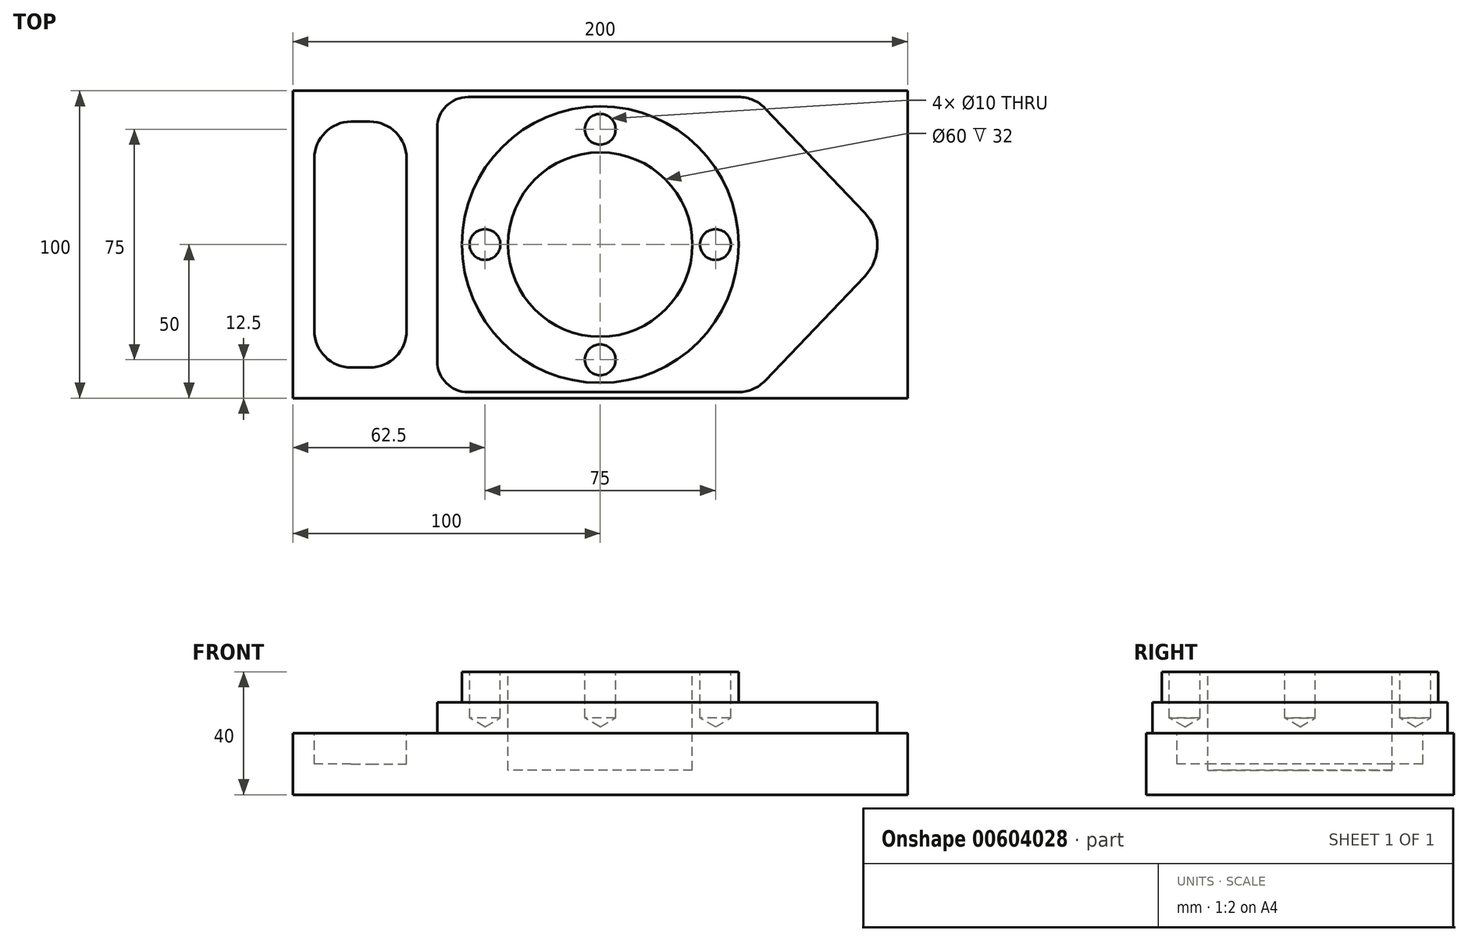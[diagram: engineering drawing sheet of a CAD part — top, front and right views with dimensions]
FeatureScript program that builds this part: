
annotation { "Feature Type Name" : "Feature", "Feature Type Description" : "" }
export const myFeature = defineFeature(function(context is Context, id is Id, definition is map)
    precondition{}
    {
        {
            var Q0;
            Q0=qCreatedBy(makeId("Top.planeOp"),FACE);
            var sketch = newSketch(context, id + "F0", { "sketchPlane" : qUnion([Q0])});
            skLineSegment(sketch, "E0.bottom", {"start": v(-100, 50) * mm, "end": v(100, 50) * mm});
            skLineSegment(sketch, "E0.top", {"start": v(-100, -50) * mm, "end": v(100, -50) * mm});
            skLineSegment(sketch, "E0.left", {"start": v(-100, 50) * mm, "end": v(-100, -50) * mm});
            skLineSegment(sketch, "E0.right", {"start": v(100, 50) * mm, "end": v(100, -50) * mm});
            skPoint(sketch, "E0.middle", {"position": v(0, 0) * mm});
            skSolve(sketch);
        }
        {
            var Q0;
            Q0=makeQuery(id+"F0.imprint","IMPRINT",FACE,{"disambiguationData":[TD([[makeQuery(id+"F0.imprint","IMPRINT",EDGE,{"derivedFrom":sQuery(id+"F0.wireOp",EDGE,"E0.bottom")}),-1.0]])]});
            extrude(context, id + "F1", {"entities" : qUnion([Q0]), "depth" : 20 * mm, "offsetDistance" : 25 * mm});
        }
        {
            var Q0;
            Q0=makeQuery(id+"F1.opExtrude","CAP_FACE",FACE,{"disambiguationData":[OSD([sQuery(id+"F0.wireOp",EDGE,"E0.bottom"),sQuery(id+"F0.wireOp",EDGE,"E0.top"),sQuery(id+"F0.wireOp",EDGE,"E0.left"),sQuery(id+"F0.wireOp",EDGE,"E0.right")])],"isStart":false});
            var sketch = newSketch(context, id + "F2", { "sketchPlane" : qUnion([Q0])});
            skLineSegment(sketch, "E1.bottom", {"start": v(-81, 40) * mm, "end": v(-75, 40) * mm});
            skLineSegment(sketch, "E1.top", {"start": v(-81, -40) * mm, "end": v(-75, -40) * mm});
            skLineSegment(sketch, "E1.left", {"start": v(-93, 28) * mm, "end": v(-93, -28) * mm});
            skLineSegment(sketch, "E1.right", {"start": v(-63, 28) * mm, "end": v(-63, -28) * mm});
            skPoint(sketch, "E2.visualSharp", {"position": v(-93, 40) * mm});
            skArc(sketch, "E2.filletArc", {"start": v(-81, 40) * mm, "mid": v(-89.49, 36.49) * mm, "end": v(-93, 28) * mm});
            skPoint(sketch, "E3.visualSharp", {"position": v(-63, 40) * mm});
            skArc(sketch, "E3.filletArc", {"start": v(-63, 28) * mm, "mid": v(-66.51, 36.49) * mm, "end": v(-75, 40) * mm});
            skPoint(sketch, "E4.visualSharp", {"position": v(-93, -40) * mm});
            skArc(sketch, "E4.filletArc", {"start": v(-93, -28) * mm, "mid": v(-89.49, -36.49) * mm, "end": v(-81, -40) * mm});
            skPoint(sketch, "E5.visualSharp", {"position": v(-63, -40) * mm});
            skArc(sketch, "E5.filletArc", {"start": v(-75, -40) * mm, "mid": v(-66.51, -36.49) * mm, "end": v(-63, -28) * mm});
            skSolve(sketch);
        }
        {
            var Q0;
            Q0=makeQuery(id+"F2.imprint","IMPRINT",FACE,{"disambiguationData":[TD([[makeQuery(id+"F2.imprint","IMPRINT",EDGE,{"derivedFrom":sQuery(id+"F2.wireOp",EDGE,"E1.bottom")}),-1.0]])]});
            extrude(context, id + "F3", {"entities" : qUnion([Q0]), "operationType" : NewBodyOperationType.REMOVE, "oppositeDirection" : true, "depth" : 10 * mm, "offsetDistance" : 25 * mm});
        }
        {
            var Q0;
            Q0=makeQuery(id+"F1.opExtrude","CAP_FACE",FACE,{"disambiguationData":[OSD([sQuery(id+"F0.wireOp",EDGE,"E0.bottom"),sQuery(id+"F0.wireOp",EDGE,"E0.top"),sQuery(id+"F0.wireOp",EDGE,"E0.left"),sQuery(id+"F0.wireOp",EDGE,"E0.right")])],"isStart":false});
            var sketch = newSketch(context, id + "F4", { "sketchPlane" : qUnion([Q0])});
            skLineSegment(sketch, "E6.bottom", {"start": v(-43, 48) * mm, "end": v(45.03, 48) * mm});
            skLineSegment(sketch, "E6.top", {"start": v(-43, -48) * mm, "end": v(45.03, -48) * mm});
            skLineSegment(sketch, "E6.left", {"start": v(-53, 38) * mm, "end": v(-53, -38) * mm});
            skPoint(sketch, "E7.visualSharp", {"position": v(-53, 48) * mm});
            skArc(sketch, "E7.filletArc", {"start": v(-43, 48) * mm, "mid": v(-50.07, 45.07) * mm, "end": v(-53, 38) * mm});
            skPoint(sketch, "E8.visualSharp", {"position": v(-53, -48) * mm});
            skArc(sketch, "E8.filletArc", {"start": v(-53, -38) * mm, "mid": v(-50.07, -45.07) * mm, "end": v(-43, -48) * mm});
            skLineSegment(sketch, "E9", {"start": v(53.72, 44.28) * mm, "end": v(86.04, 10.35) * mm});
            skLineSegment(sketch, "E10", {"start": v(53.72, -44.28) * mm, "end": v(86.04, -10.35) * mm});
            skArc(sketch, "E11", {"start": v(86.04, -10.35) * mm, "mid": v(90.18, 0) * mm, "end": v(86.04, 10.35) * mm});
            skArc(sketch, "E12", {"start": v(53.72, 44.28) * mm, "mid": v(49.75, 47.03) * mm, "end": v(45.03, 48) * mm});
            skArc(sketch, "E13", {"start": v(45.03, -48) * mm, "mid": v(49.75, -47.03) * mm, "end": v(53.72, -44.28) * mm});
            skSolve(sketch);
        }
        {
            var Q0;
            Q0=makeQuery(id+"F4.imprint","IMPRINT",FACE,{"disambiguationData":[TD([[makeQuery(id+"F4.imprint","IMPRINT",EDGE,{"derivedFrom":sQuery(id+"F4.wireOp",EDGE,"E6.bottom")}),-1.0]])]});
            extrude(context, id + "F5", {"entities" : qUnion([Q0]), "operationType" : NewBodyOperationType.ADD, "depth" : 10 * mm, "offsetDistance" : 25 * mm});
        }
        {
            var Q0;
            Q0=makeQuery(id+"F5.opExtrude","CAP_FACE",FACE,{"disambiguationData":[OSD([sQuery(id+"F4.wireOp",EDGE,"E6.bottom"),sQuery(id+"F4.wireOp",EDGE,"E6.top"),sQuery(id+"F4.wireOp",EDGE,"E6.left"),sQuery(id+"F4.wireOp",EDGE,"E7.filletArc"),sQuery(id+"F4.wireOp",EDGE,"E8.filletArc"),sQuery(id+"F4.wireOp",EDGE,"E9"),sQuery(id+"F4.wireOp",EDGE,"E10"),sQuery(id+"F4.wireOp",EDGE,"E11"),sQuery(id+"F4.wireOp",EDGE,"E12"),sQuery(id+"F4.wireOp",EDGE,"E13")])],"isStart":false});
            var sketch = newSketch(context, id + "F6", { "sketchPlane" : qUnion([Q0])});
            skCircle(sketch, "E14", {"center": v(0, 0) * mm, "radius": 45 * mm});
            skSolve(sketch);
        }
        {
            var Q0;
            Q0=makeQuery(id+"F6.imprint","IMPRINT",FACE,{"disambiguationData":[TD([[makeQuery(id+"F6.imprint","IMPRINT",EDGE,{"derivedFrom":sQuery(id+"F6.wireOp",EDGE,"E14")}),1.0]])]});
            extrude(context, id + "F7", {"entities" : qUnion([Q0]), "operationType" : NewBodyOperationType.ADD, "depth" : 10 * mm, "offsetDistance" : 25 * mm});
        }
        {
            var Q0;
            Q0=makeQuery(id+"F7.opExtrude","CAP_FACE",FACE,{"disambiguationData":[OSD([sQuery(id+"F6.wireOp",EDGE,"E14")])],"isStart":false});
            var sketch = newSketch(context, id + "F8", { "sketchPlane" : qUnion([Q0])});
            skCircle(sketch, "E15", {"center": v(0, 0) * mm, "radius": 30 * mm});
            skSolve(sketch);
        }
        {
            var Q0;
            Q0=makeQuery(id+"F8.imprint","IMPRINT",FACE,{"disambiguationData":[TD([[makeQuery(id+"F8.imprint","IMPRINT",EDGE,{"derivedFrom":sQuery(id+"F8.wireOp",EDGE,"E15")}),1.0]])]});
            extrude(context, id + "F9", {"entities" : qUnion([Q0]), "operationType" : NewBodyOperationType.REMOVE, "oppositeDirection" : true, "depth" : 32 * mm, "offsetDistance" : 25 * mm});
        }
        {
            var Q0;
            Q0=makeQuery(id+"F7.opExtrude","CAP_FACE",FACE,{"disambiguationData":[OSD([sQuery(id+"F6.wireOp",EDGE,"E14")])],"isStart":false});
            var sketch = newSketch(context, id + "F10", { "sketchPlane" : qUnion([Q0])});
            skCircle(sketch, "E16", {"center": v(0, 0) * mm, "radius": 37.5 * mm, "construction": true});
            skCircle(sketch, "E17", {"center": v(-37.5, 0) * mm, "radius": 5 * mm});
            skCircle(sketch, "E18", {"center": v(0, 37.5) * mm, "radius": 5 * mm});
            skCircle(sketch, "E19", {"center": v(37.5, 0) * mm, "radius": 5 * mm});
            skCircle(sketch, "E20", {"center": v(0, -37.5) * mm, "radius": 5 * mm});
            skSolve(sketch);
        }
        {
            var Q0;
            Q0=sQuery(id+"F10.wireOp",VERTEX,"E17.center");
            var Q1;
            Q1=sQuery(id+"F10.wireOp",VERTEX,"E18.center");
            var Q2;
            Q2=sQuery(id+"F10.wireOp",VERTEX,"E19.center");
            var Q3;
            Q3=sQuery(id+"F10.wireOp",VERTEX,"E20.center");
            var Q4;
            Q4=makeQuery(id+"F1.opExtrude","SWEPT_BODY",BODY,{"disambiguationData":[OSD([sQuery(id+"F0.wireOp",EDGE,"E0.bottom"),sQuery(id+"F0.wireOp",EDGE,"E0.top"),sQuery(id+"F0.wireOp",EDGE,"E0.left"),sQuery(id+"F0.wireOp",EDGE,"E0.right")])]});
            hole(context, id + "F11", {"style" : HoleStyle.SIMPLE, "endStyle" : HoleEndStyle.BLIND, "holeDiameter" : 10 * mm, "majorDiameter" : 5 * mm, "holeDepth" : 15 * mm, "isTappedThrough" : true, "tappedDepth" : 12 * mm, "tapClearance" : 3, "locations" : qUnion([Q0, Q1, Q2, Q3]), "scope" : qUnion([Q4])});
        }
    });
